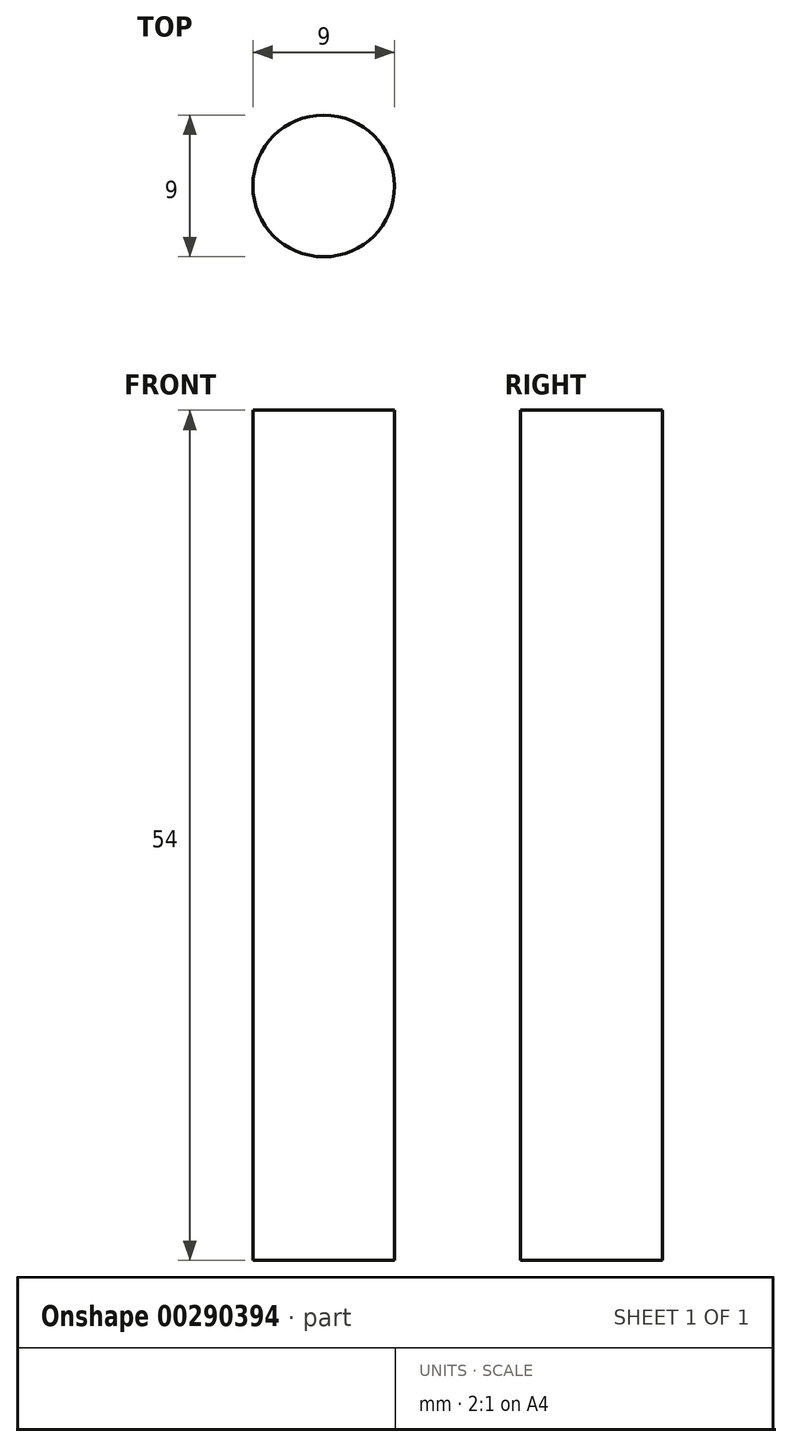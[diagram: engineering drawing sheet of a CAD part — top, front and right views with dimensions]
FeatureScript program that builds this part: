
annotation { "Feature Type Name" : "Feature", "Feature Type Description" : "" }
export const myFeature = defineFeature(function(context is Context, id is Id, definition is map)
    precondition{}
    {
        {
            var Q0;
            Q0=qCreatedBy(makeId("Front.planeOp"),FACE);
            var sketch = newSketch(context, id + "F0", { "sketchPlane" : qUnion([Q0])});
            skLineSegment(sketch, "E0.bottom", {"start": v(0, 0) * mm, "end": v(4.5, 0) * mm});
            skLineSegment(sketch, "E0.top", {"start": v(0, 54) * mm, "end": v(4.5, 54) * mm});
            skLineSegment(sketch, "E0.left", {"start": v(0, 0) * mm, "end": v(0, 54) * mm});
            skLineSegment(sketch, "E0.right", {"start": v(4.5, 0) * mm, "end": v(4.5, 54) * mm});
            skSolve(sketch);
        }
        {
            var Q0;
            Q0=makeQuery(id+"F0.imprint","IMPRINT",FACE,{"disambiguationData":[TD([[makeQuery(id+"F0.imprint","IMPRINT",EDGE,{"derivedFrom":sQuery(id+"F0.wireOp",EDGE,"E0.bottom")}),1.0]])]});
            var Q1;
            Q1=sQuery(id+"F0.wireOp",EDGE,"E0.left");
            revolve(context, id + "F1", {"entities" : qUnion([Q0]), "axis" : qUnion([Q1]), "revolveType" : RevolveType.FULL});
        }
    });
